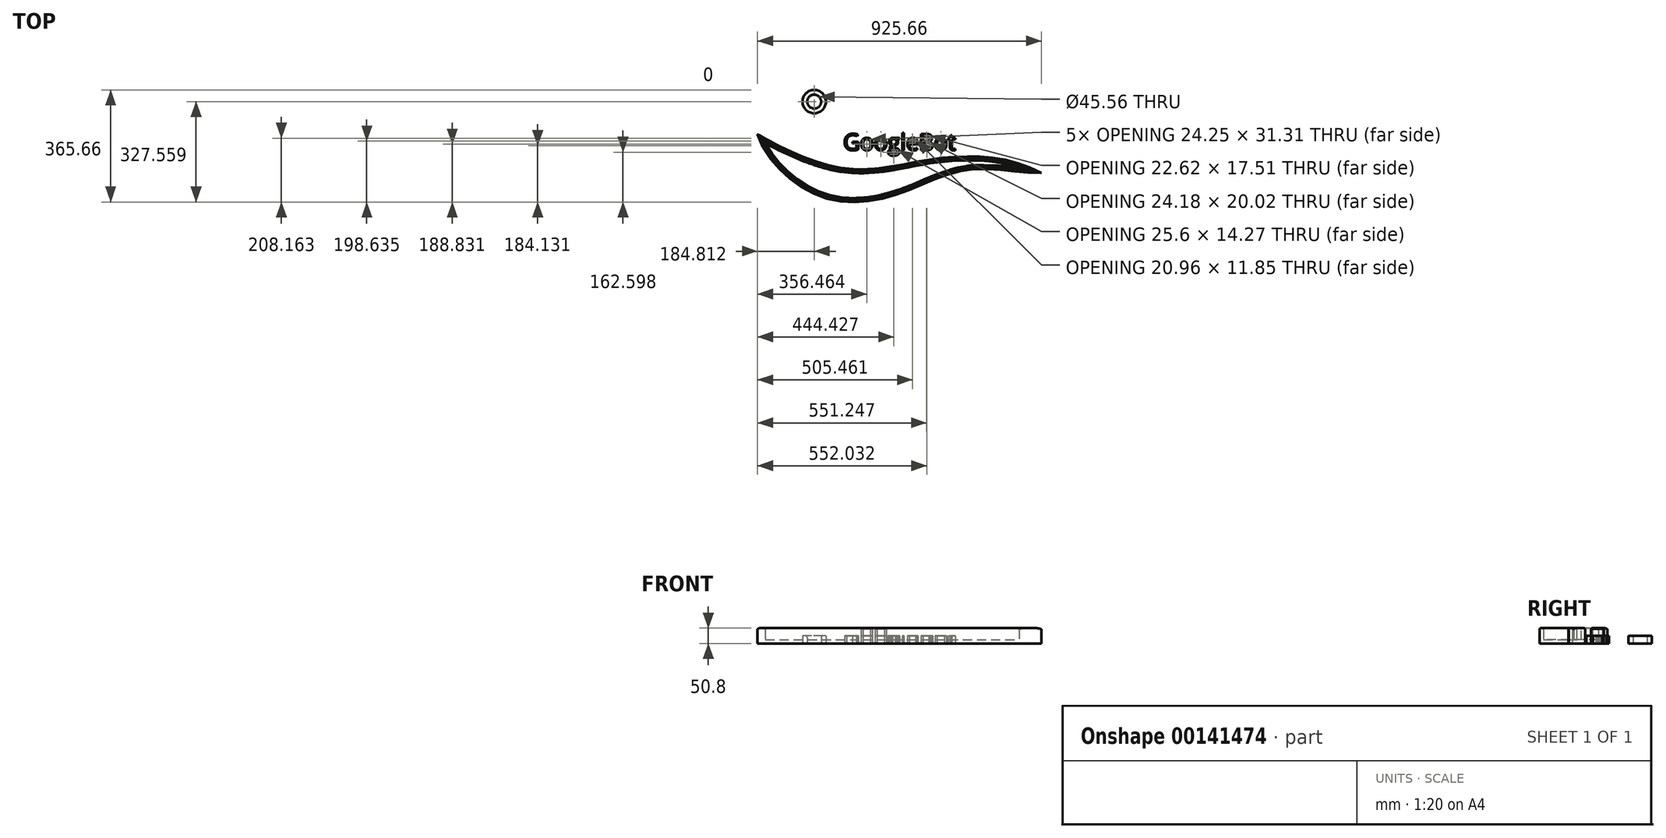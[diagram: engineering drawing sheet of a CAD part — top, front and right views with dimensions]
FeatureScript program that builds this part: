
annotation { "Feature Type Name" : "Feature", "Feature Type Description" : "" }
export const myFeature = defineFeature(function(context is Context, id is Id, definition is map)
    precondition{}
    {
        {
            var Q0;
            Q0=qCreatedBy(makeId("Top.planeOp"),FACE);
            var sketch = newSketch(context, id + "F0", { "sketchPlane" : qUnion([Q0])});
            skText(sketch, "E0", { "text": "GoogleBot", "fontName": "OpenSans-Regular.ttf"});
            const initialGuessF0  = {"E0": [-0.06782, -0.01606, 1, 0, 0.05394]};
            skSetInitialGuess(sketch, initialGuessF0);
            skSolve(sketch);
        }
        {
            var Q0;
            Q0 = qSketchRegion(id + "F0", true);
            extrude(context, id + "F1", {"entities" : qUnion([Q0]), "depth" : 25.4 * mm});
        }
        {
            var Q0;
            Q0=qCreatedBy(makeId("Top.planeOp"),FACE);
            var sketch = newSketch(context, id + "F2", { "sketchPlane" : qUnion([Q0])});
            skFitSpline(sketch, "E1", {"points": [v(-347.12, 36.2) * mm, v(-67.2, -74.64) * mm, v(220.64, -45.28) * mm, v(458.15, -46.85) * mm, v(578.54, -89.86) * mm], "startDerivative": vector(634.73, -375.84) * mm, "endDerivative": vector(553.86, -252.46) * mm});
            skFitSpline(sketch, "E2", {"points": [v(-347.12, 36.2) * mm, v(-139.25, -167.4) * mm, v(134.74, -150.58) * mm, v(348.51, -78.5) * mm, v(578.54, -89.86) * mm], "startDerivative": vector(259.06, -877.1) * mm, "endDerivative": vector(750.24, 34.11) * mm});
            skCircle(sketch, "E3", {"center": v(-162.3, 142.68) * mm, "radius": 38.1 * mm});
            skCircle(sketch, "E4", {"center": v(-162.3, 142.68) * mm, "radius": 22.78 * mm});
            skSolve(sketch);
        }
        {
            var Q0;
            Q0=makeQuery(id+"F2.imprint","IMPRINT",FACE,{"disambiguationData":[TD([[makeQuery(id+"F2.imprint","IMPRINT",EDGE,{"derivedFrom":sQuery(id+"F2.wireOp",EDGE,"E3")}),1.0]])]});
            extrude(context, id + "F3", {"entities" : qUnion([Q0]), "depth" : 25.4 * mm});
        }
        {
            var Q0;
            Q0=makeQuery(id+"F3.opExtrude","SWEPT_FACE",FACE,{"disambiguationData":[OSD([sQuery(id+"F2.wireOp",EDGE,"E4")])]});
            fillet(context, id + "F4", {"entities" : qUnion([Q0]), "radius" : 5.08 * mm, "tangentPropagation" : true, "allowEdgeOverflow" : false});
        }
        {
            var Q0;
            Q0=makeQuery(id+"F2.imprint","IMPRINT",FACE,{"disambiguationData":[TD([[makeQuery(id+"F2.imprint","IMPRINT",EDGE,{"derivedFrom":sQuery(id+"F2.wireOp",EDGE,"E1")}),-1.0]])]});
            extrude(context, id + "F5", {"entities" : qUnion([Q0]), "operationType" : NewBodyOperationType.ADD, "depth" : 25.4 * mm});
        }
        {
            var Q0;
            Q0=makeQuery(id+"F1.opExtrude","CAP_FACE",FACE,{"disambiguationData":[OSD([sQuery(id+"F0.wireOp",EDGE,"E0.sketch_text.stroke-20"),sQuery(id+"F0.wireOp",EDGE,"E0.sketch_text.stroke-21"),sQuery(id+"F0.wireOp",EDGE,"E0.sketch_text.stroke-22"),sQuery(id+"F0.wireOp",EDGE,"E0.sketch_text.stroke-23"),sQuery(id+"F0.wireOp",EDGE,"E0.sketch_text.stroke-24"),sQuery(id+"F0.wireOp",EDGE,"E0.sketch_text.stroke-25"),sQuery(id+"F0.wireOp",EDGE,"E0.sketch_text.stroke-26"),sQuery(id+"F0.wireOp",EDGE,"E0.sketch_text.stroke-27"),sQuery(id+"F0.wireOp",EDGE,"E0.sketch_text.stroke-28"),sQuery(id+"F0.wireOp",EDGE,"E0.sketch_text.stroke-29"),sQuery(id+"F0.wireOp",EDGE,"E0.sketch_text.stroke-30"),sQuery(id+"F0.wireOp",EDGE,"E0.sketch_text.stroke-31"),sQuery(id+"F0.wireOp",EDGE,"E0.sketch_text.stroke-32"),sQuery(id+"F0.wireOp",EDGE,"E0.sketch_text.stroke-33"),sQuery(id+"F0.wireOp",EDGE,"E0.sketch_text.stroke-34"),sQuery(id+"F0.wireOp",EDGE,"E0.sketch_text.stroke-35"),sQuery(id+"F0.wireOp",EDGE,"E0.sketch_text.stroke-36")])],"isStart":false});
            var Q1;
            Q1=makeQuery(id+"F1.opExtrude","CAP_FACE",FACE,{"disambiguationData":[OSD([sQuery(id+"F0.wireOp",EDGE,"E0.sketch_text.stroke-37"),sQuery(id+"F0.wireOp",EDGE,"E0.sketch_text.stroke-38"),sQuery(id+"F0.wireOp",EDGE,"E0.sketch_text.stroke-39"),sQuery(id+"F0.wireOp",EDGE,"E0.sketch_text.stroke-40"),sQuery(id+"F0.wireOp",EDGE,"E0.sketch_text.stroke-41"),sQuery(id+"F0.wireOp",EDGE,"E0.sketch_text.stroke-42"),sQuery(id+"F0.wireOp",EDGE,"E0.sketch_text.stroke-43"),sQuery(id+"F0.wireOp",EDGE,"E0.sketch_text.stroke-44"),sQuery(id+"F0.wireOp",EDGE,"E0.sketch_text.stroke-45"),sQuery(id+"F0.wireOp",EDGE,"E0.sketch_text.stroke-46"),sQuery(id+"F0.wireOp",EDGE,"E0.sketch_text.stroke-47"),sQuery(id+"F0.wireOp",EDGE,"E0.sketch_text.stroke-48"),sQuery(id+"F0.wireOp",EDGE,"E0.sketch_text.stroke-49"),sQuery(id+"F0.wireOp",EDGE,"E0.sketch_text.stroke-50"),sQuery(id+"F0.wireOp",EDGE,"E0.sketch_text.stroke-51"),sQuery(id+"F0.wireOp",EDGE,"E0.sketch_text.stroke-52"),sQuery(id+"F0.wireOp",EDGE,"E0.sketch_text.stroke-53")])],"isStart":false});
            extrude(context, id + "F6", {"entities" : qUnion([Q0, Q1]), "depth" : 25.4 * mm});
        }
        {
            var Q0;
            Q0=makeQuery(id+"F5.opExtrude","CAP_FACE",FACE,{"disambiguationData":[OSD([sQuery(id+"F2.wireOp",EDGE,"E1"),sQuery(id+"F2.wireOp",EDGE,"E2")])],"isStart":false});
            extrude(context, id + "F7", {"entities" : qUnion([Q0]), "operationType" : NewBodyOperationType.ADD, "depth" : 25.4 * mm});
        }
        {
            var Q0;
            Q0=makeQuery(id+"F7.opExtrude","CAP_FACE",FACE,{"disambiguationData":[OSD([sQuery(id+"F2.wireOp",EDGE,"E1"),sQuery(id+"F2.wireOp",EDGE,"E2")])],"isStart":false});
            shell(context, id + "F8", {"entities" : qUnion([Q0]), "thickness" : 12.7 * mm});
        }
        {
            var Q0;
            Q0=makeQuery(id+"F7.opExtrude","CAP_EDGE",EDGE,{"disambiguationData":[OSD([sQuery(id+"F2.wireOp",EDGE,"E1")])],"isStart":false});
            var Q1;
            Q1=makeQuery(id+"F7.opExtrude","CAP_EDGE",EDGE,{"disambiguationData":[OSD([sQuery(id+"F2.wireOp",EDGE,"E2")])],"isStart":false});
            var Q2;
            Q2=makeQuery(id+"F7.opExtrude","CAP_FACE",FACE,{"disambiguationData":[OSD([sQuery(id+"F2.wireOp",EDGE,"E1"),sQuery(id+"F2.wireOp",EDGE,"E2")])],"isStart":false});
            fillet(context, id + "F9", {"entities" : qUnion([Q0, Q1, Q2]), "radius" : 5.08 * mm, "tangentPropagation" : true, "allowEdgeOverflow" : false});
        }
        {
            var Q0;
            Q0=makeQuery(id+"F6.opExtrude","CAP_EDGE",EDGE,{"disambiguationData":[OSD([sQuery(id+"F0.wireOp",EDGE,"E0.sketch_text.stroke-23")])],"isStart":false});
            var Q1;
            Q1=makeQuery(id+"F6.opExtrude","CAP_EDGE",EDGE,{"disambiguationData":[OSD([sQuery(id+"F0.wireOp",EDGE,"E0.sketch_text.stroke-39")])],"isStart":false});
            chamfer(context, id + "F10", {"entities" : qUnion([Q0, Q1]), "width" : 2.54 * mm, "tangentPropagation" : true});
        }
    });
